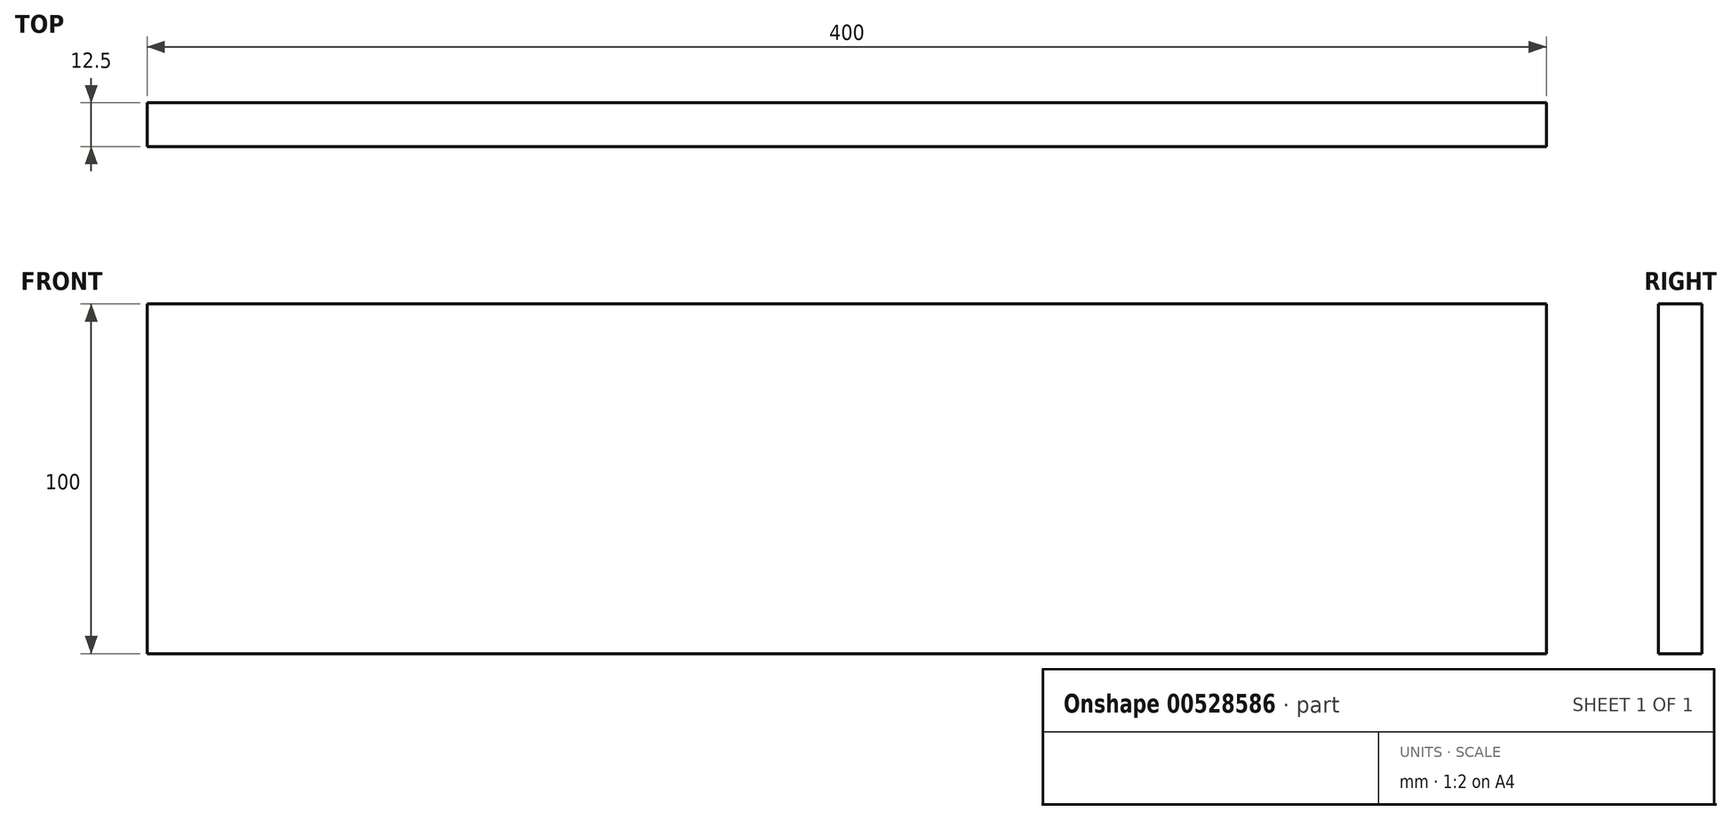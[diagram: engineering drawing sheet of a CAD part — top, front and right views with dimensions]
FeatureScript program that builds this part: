
annotation { "Feature Type Name" : "Feature", "Feature Type Description" : "" }
export const myFeature = defineFeature(function(context is Context, id is Id, definition is map)
    precondition{}
    {
        {
            var Q0;
            Q0=qCreatedBy(makeId("Front.planeOp"),FACE);
            var sketch = newSketch(context, id + "F0", { "sketchPlane" : qUnion([Q0])});
            skLineSegment(sketch, "E0.bottom", {"start": v(0, 100) * mm, "end": v(400, 100) * mm});
            skLineSegment(sketch, "E0.top", {"start": v(0, 0) * mm, "end": v(400, 0) * mm});
            skLineSegment(sketch, "E0.left", {"start": v(0, 100) * mm, "end": v(0, 0) * mm});
            skLineSegment(sketch, "E0.right", {"start": v(400, 100) * mm, "end": v(400, 0) * mm});
            skSolve(sketch);
        }
        {
            var Q0;
            Q0 = qSketchRegion(id + "F0", true);
            extrude(context, id + "F1", {"entities" : qUnion([Q0]), "depth" : 12.5 * mm, "offsetDistance" : 25 * mm});
        }
    });
